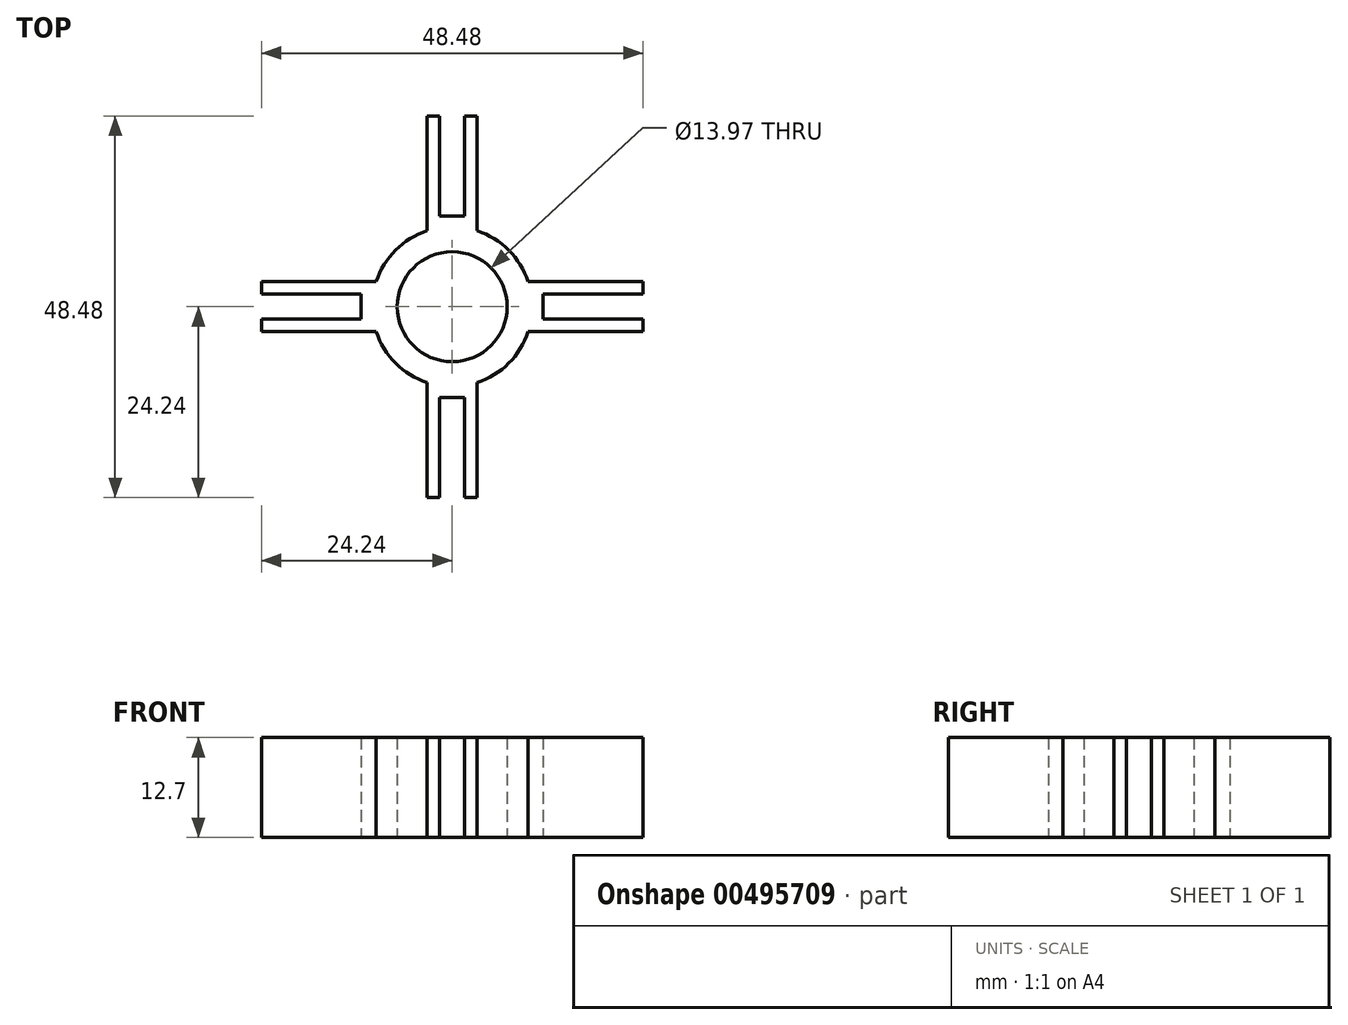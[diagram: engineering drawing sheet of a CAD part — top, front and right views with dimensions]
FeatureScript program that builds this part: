
annotation { "Feature Type Name" : "Feature", "Feature Type Description" : "" }
export const myFeature = defineFeature(function(context is Context, id is Id, definition is map)
    precondition{}
    {
        {
            var Q0;
            Q0=qCreatedBy(makeId("Top.planeOp"),FACE);
            var sketch = newSketch(context, id + "F0", { "sketchPlane" : qUnion([Q0])});
            skCircle(sketch, "E0", {"center": v(0, 0) * mm, "radius": 6.99 * mm});
            skCircle(sketch, "E1", {"center": v(0, 0) * mm, "radius": 10.16 * mm});
            skLineSegment(sketch, "E2.bottom", {"start": v(-3.18, 24.24) * mm, "end": v(-1.59, 24.24) * mm});
            skLineSegment(sketch, "E2.top", {"start": v(-3.17, 7.73) * mm, "end": v(3.17, 7.73) * mm});
            skLineSegment(sketch, "E2.left", {"start": v(-3.18, 24.24) * mm, "end": v(-3.17, 7.73) * mm});
            skLineSegment(sketch, "E2.right", {"start": v(3.18, 24.24) * mm, "end": v(3.17, 7.73) * mm});
            skPoint(sketch, "E3", {"position": v(0, 24.24) * mm});
            skLineSegment(sketch, "E4.top", {"start": v(-1.59, 11.55) * mm, "end": v(1.59, 11.55) * mm});
            skLineSegment(sketch, "E4.left", {"start": v(-1.59, 24.24) * mm, "end": v(-1.59, 11.55) * mm});
            skLineSegment(sketch, "E4.right", {"start": v(1.59, 24.24) * mm, "end": v(1.59, 11.55) * mm});
            skLineSegment(sketch, "E5.trimOffspring", {"start": v(1.59, 24.24) * mm, "end": v(3.18, 24.24) * mm});
            skLineSegment(sketch, "E6.1.0", {"start": v(-24.24, -1.59) * mm, "end": v(-11.55, -1.59) * mm});
            skLineSegment(sketch, "E6.1.1", {"start": v(-24.24, 1.59) * mm, "end": v(-11.55, 1.59) * mm});
            skLineSegment(sketch, "E6.1.2", {"start": v(-11.55, -1.59) * mm, "end": v(-11.55, 1.59) * mm});
            skPoint(sketch, "E6.1.3", {"position": v(-24.24, 0) * mm});
            skPoint(sketch, "E6.1.4", {"position": v(-24.24, 0) * mm});
            skLineSegment(sketch, "E6.1.5", {"start": v(-24.24, 1.59) * mm, "end": v(-24.24, 3.18) * mm});
            skLineSegment(sketch, "E6.1.6", {"start": v(-24.24, -3.17) * mm, "end": v(-24.24, -1.59) * mm});
            skLineSegment(sketch, "E6.1.7", {"start": v(-7.73, -3.17) * mm, "end": v(-7.73, 3.17) * mm});
            skLineSegment(sketch, "E6.1.8", {"start": v(-24.24, 3.18) * mm, "end": v(-7.73, 3.17) * mm});
            skLineSegment(sketch, "E6.1.9", {"start": v(-24.24, -3.17) * mm, "end": v(-7.73, -3.17) * mm});
            skLineSegment(sketch, "E6.2.0", {"start": v(1.59, -24.24) * mm, "end": v(1.59, -11.55) * mm});
            skLineSegment(sketch, "E6.2.1", {"start": v(-1.59, -24.24) * mm, "end": v(-1.59, -11.55) * mm});
            skLineSegment(sketch, "E6.2.2", {"start": v(1.59, -11.55) * mm, "end": v(-1.59, -11.55) * mm});
            skPoint(sketch, "E6.2.3", {"position": v(0, -24.24) * mm});
            skPoint(sketch, "E6.2.4", {"position": v(0, -24.24) * mm});
            skLineSegment(sketch, "E6.2.5", {"start": v(-1.59, -24.24) * mm, "end": v(-3.18, -24.24) * mm});
            skLineSegment(sketch, "E6.2.6", {"start": v(3.17, -24.24) * mm, "end": v(1.59, -24.24) * mm});
            skLineSegment(sketch, "E6.2.7", {"start": v(3.17, -7.73) * mm, "end": v(-3.18, -7.73) * mm});
            skLineSegment(sketch, "E6.2.8", {"start": v(-3.18, -24.24) * mm, "end": v(-3.18, -7.73) * mm});
            skLineSegment(sketch, "E6.2.9", {"start": v(3.17, -24.24) * mm, "end": v(3.17, -7.73) * mm});
            skLineSegment(sketch, "E6.3.0", {"start": v(24.24, 1.59) * mm, "end": v(11.55, 1.59) * mm});
            skLineSegment(sketch, "E6.3.1", {"start": v(24.24, -1.59) * mm, "end": v(11.55, -1.59) * mm});
            skLineSegment(sketch, "E6.3.2", {"start": v(11.55, 1.59) * mm, "end": v(11.55, -1.59) * mm});
            skPoint(sketch, "E6.3.3", {"position": v(24.24, 0) * mm});
            skPoint(sketch, "E6.3.4", {"position": v(24.24, 0) * mm});
            skLineSegment(sketch, "E6.3.5", {"start": v(24.24, -1.59) * mm, "end": v(24.24, -3.18) * mm});
            skLineSegment(sketch, "E6.3.6", {"start": v(24.24, 3.17) * mm, "end": v(24.24, 1.59) * mm});
            skLineSegment(sketch, "E6.3.7", {"start": v(7.73, 3.17) * mm, "end": v(7.73, -3.18) * mm});
            skLineSegment(sketch, "E6.3.8", {"start": v(24.24, -3.18) * mm, "end": v(7.73, -3.18) * mm});
            skLineSegment(sketch, "E6.3.9", {"start": v(24.24, 3.17) * mm, "end": v(7.73, 3.17) * mm});
            skSolve(sketch);
        }
        {
            var Q0;
            {var subQ6=sQuery(id+"F0.wireOp",EDGE,"E2.bottom");Q0=makeQuery(id+"F0.imprint","IMPRINT",FACE,{"disambiguationData":[TD([[makeQuery(id+"F0.imprint","IMPRINT",EDGE,{"derivedFrom":subQ6}),-1.0]])]});}
            var Q1;
            {var subQ5=sQuery(id+"F0.wireOp",EDGE,"E2.top");Q1=makeQuery(id+"F0.imprint","IMPRINT",FACE,{"disambiguationData":[TD([[makeQuery(id+"F0.imprint","IMPRINT",EDGE,{"derivedFrom":subQ5}),1.0]])]});}
            var Q2;
            Q2=makeQuery(id+"F0.imprint","IMPRINT",FACE,{"disambiguationData":[TD([[makeQuery(id+"F0.imprint","IMPRINT",EDGE,{"derivedFrom":sQuery(id+"F0.wireOp",EDGE,"E0")}),-1.0]])]});
            var Q3;
            {var subQ5=sQuery(id+"F0.wireOp",EDGE,"E6.3.7");Q3=makeQuery(id+"F0.imprint","IMPRINT",FACE,{"disambiguationData":[TD([[makeQuery(id+"F0.imprint","IMPRINT",EDGE,{"derivedFrom":subQ5}),1.0]])]});}
            var Q4;
            Q4=makeQuery(id+"F0.imprint","IMPRINT",FACE,{"disambiguationData":[TD([[makeQuery(id+"F0.imprint","IMPRINT",EDGE,{"derivedFrom":sQuery(id+"F0.wireOp",EDGE,"E6.3.0")}),-1.0]])]});
            var Q5;
            Q5=makeQuery(id+"F0.imprint","IMPRINT",FACE,{"disambiguationData":[TD([[makeQuery(id+"F0.imprint","IMPRINT",EDGE,{"derivedFrom":sQuery(id+"F0.wireOp",EDGE,"E6.2.0")}),-1.0]])]});
            var Q6;
            {var subQ5=sQuery(id+"F0.wireOp",EDGE,"E6.2.7");Q6=makeQuery(id+"F0.imprint","IMPRINT",FACE,{"disambiguationData":[TD([[makeQuery(id+"F0.imprint","IMPRINT",EDGE,{"derivedFrom":subQ5}),1.0]])]});}
            var Q7;
            {var subQ5=sQuery(id+"F0.wireOp",EDGE,"E6.1.7");Q7=makeQuery(id+"F0.imprint","IMPRINT",FACE,{"disambiguationData":[TD([[makeQuery(id+"F0.imprint","IMPRINT",EDGE,{"derivedFrom":subQ5}),1.0]])]});}
            var Q8;
            Q8=makeQuery(id+"F0.imprint","IMPRINT",FACE,{"disambiguationData":[TD([[makeQuery(id+"F0.imprint","IMPRINT",EDGE,{"derivedFrom":sQuery(id+"F0.wireOp",EDGE,"E6.1.0")}),-1.0]])]});
            extrude(context, id + "F1", {"entities" : qUnion([Q0, Q1, Q2, Q3, Q4, Q5, Q6, Q7, Q8]), "depth" : 12.7 * mm});
        }
    });
